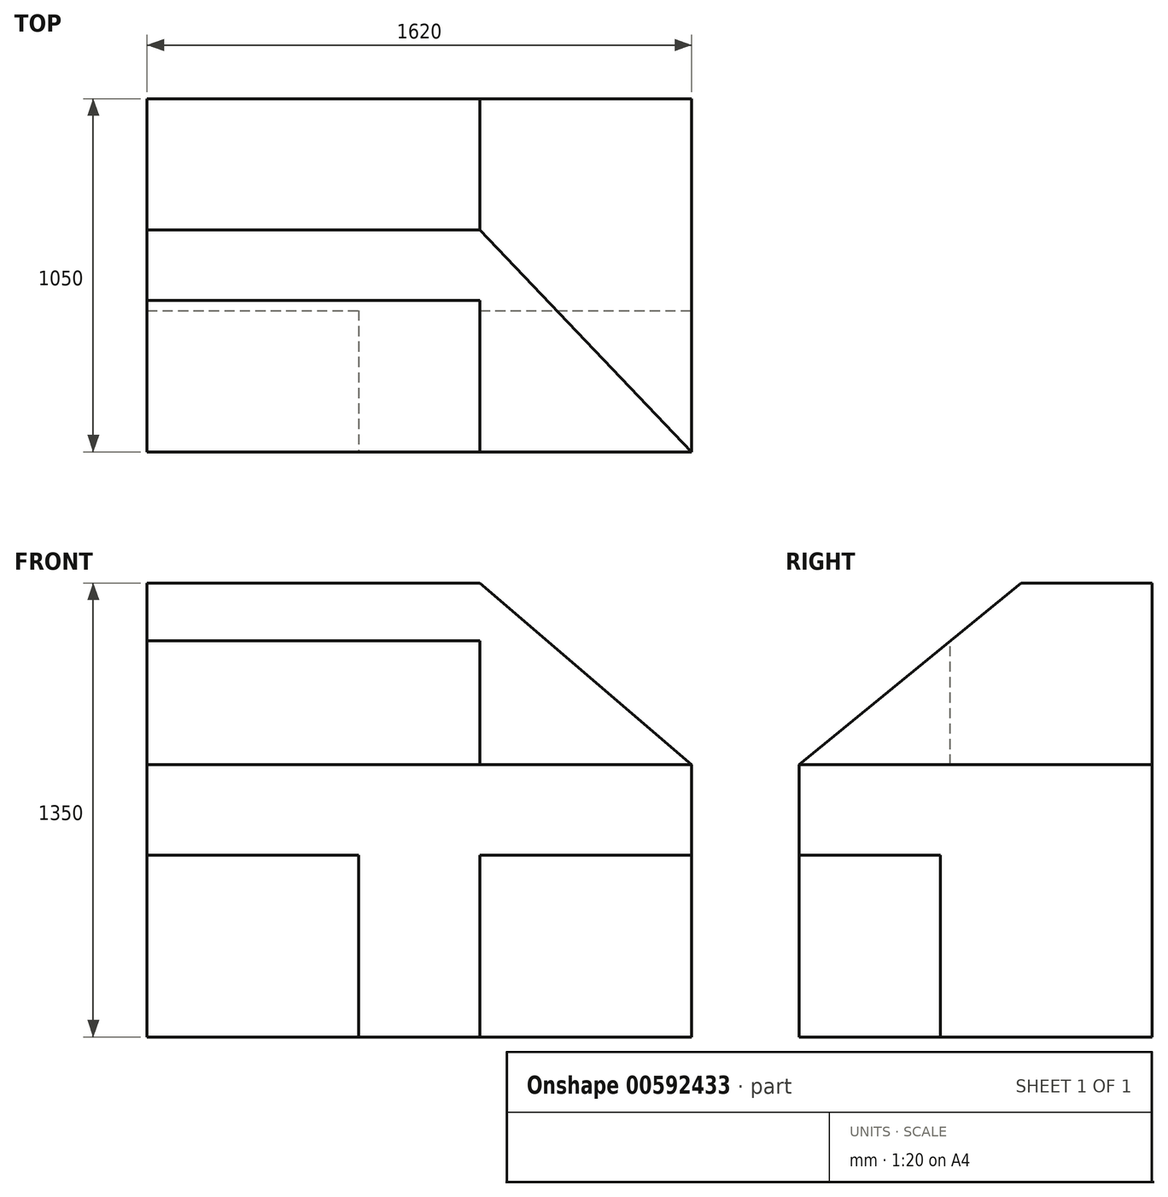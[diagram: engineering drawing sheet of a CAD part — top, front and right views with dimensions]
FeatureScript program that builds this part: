
annotation { "Feature Type Name" : "Feature", "Feature Type Description" : "" }
export const myFeature = defineFeature(function(context is Context, id is Id, definition is map)
    precondition{}
    {
        {
            var Q0;
            Q0=qCreatedBy(makeId("Front.planeOp"),FACE);
            var sketch = newSketch(context, id + "F0", { "sketchPlane" : qUnion([Q0])});
            skLineSegment(sketch, "E0.bottom", {"start": v(-810, 675) * mm, "end": v(810, 675) * mm});
            skLineSegment(sketch, "E0.top", {"start": v(-810, -675) * mm, "end": v(810, -675) * mm});
            skLineSegment(sketch, "E0.left", {"start": v(-810, 675) * mm, "end": v(-810, -675) * mm});
            skLineSegment(sketch, "E0.right", {"start": v(810, 675) * mm, "end": v(810, -675) * mm});
            skSolve(sketch);
        }
        {
            var Q0;
            Q0 = qSketchRegion(id + "F0", true);
            extrude(context, id + "F1", {"entities" : qUnion([Q0]), "depth" : 1050 * mm, "offsetDistance" : 25 * mm, "symmetric" : true});
        }
        {
            var Q0;
            Q0=makeQuery(id+"F1.opExtrude","CAP_FACE",FACE,{"disambiguationData":[OSD([sQuery(id+"F0.wireOp",EDGE,"E0.bottom"),sQuery(id+"F0.wireOp",EDGE,"E0.top"),sQuery(id+"F0.wireOp",EDGE,"E0.left"),sQuery(id+"F0.wireOp",EDGE,"E0.right")])],"isStart":false});
            var sketch = newSketch(context, id + "F2", { "sketchPlane" : qUnion([Q0])});
            skLineSegment(sketch, "E1.bottom", {"start": v(-810, -675) * mm, "end": v(-180, -675) * mm});
            skLineSegment(sketch, "E1.top", {"start": v(-810, -135) * mm, "end": v(-180, -135) * mm});
            skLineSegment(sketch, "E1.left", {"start": v(-810, -675) * mm, "end": v(-810, -135) * mm});
            skLineSegment(sketch, "E1.right", {"start": v(-180, -675) * mm, "end": v(-180, -135) * mm});
            skLineSegment(sketch, "E2.bottom", {"start": v(810, -675) * mm, "end": v(180, -675) * mm});
            skLineSegment(sketch, "E2.top", {"start": v(810, -135) * mm, "end": v(180, -135) * mm});
            skLineSegment(sketch, "E2.left", {"start": v(810, -675) * mm, "end": v(810, -135) * mm});
            skLineSegment(sketch, "E2.right", {"start": v(180, -675) * mm, "end": v(180, -135) * mm});
            skSolve(sketch);
        }
        {
            var Q0;
            Q0 = qSketchRegion(id + "F2", true);
            extrude(context, id + "F3", {"entities" : qUnion([Q0]), "operationType" : NewBodyOperationType.REMOVE, "oppositeDirection" : true, "depth" : 420 * mm, "offsetDistance" : 25 * mm});
        }
        {
            var Q0;
            Q0=makeQuery(id+"F1.opExtrude","SWEPT_FACE",FACE,{"disambiguationData":[OSD([sQuery(id+"F0.wireOp",EDGE,"E0.bottom")])]});
            var sketch = newSketch(context, id + "F4", { "sketchPlane" : qUnion([Q0])});
            skLineSegment(sketch, "E3.bottom", {"start": v(-810, -525) * mm, "end": v(180, -525) * mm});
            skLineSegment(sketch, "E3.top", {"start": v(-810, -75) * mm, "end": v(180, -75) * mm});
            skLineSegment(sketch, "E3.left", {"start": v(-810, -525) * mm, "end": v(-810, -75) * mm});
            skLineSegment(sketch, "E3.right", {"start": v(180, -525) * mm, "end": v(180, -75) * mm});
            skSolve(sketch);
        }
        {
            var Q0;
            Q0 = qSketchRegion(id + "F4", true);
            extrude(context, id + "F5", {"entities" : qUnion([Q0]), "operationType" : NewBodyOperationType.REMOVE, "oppositeDirection" : true, "depth" : 540 * mm, "offsetDistance" : 25 * mm});
        }
        {
            var Q0;
            Q0=makeQuery(id+"F1.opExtrude","SWEPT_FACE",FACE,{"disambiguationData":[OSD([sQuery(id+"F0.wireOp",EDGE,"E0.right")])]});
            var sketch = newSketch(context, id + "F6", { "sketchPlane" : qUnion([Q0])});
            skLineSegment(sketch, "E4", {"start": v(-525, 675) * mm, "end": v(-525, 135) * mm});
            skLineSegment(sketch, "E5", {"start": v(-525, 135) * mm, "end": v(135, 675) * mm});
            skLineSegment(sketch, "E6", {"start": v(135, 675) * mm, "end": v(-525, 675) * mm});
            skSolve(sketch);
        }
        {
            var Q0;
            Q0 = qSketchRegion(id + "F6", true);
            extrude(context, id + "F7", {"entities" : qUnion([Q0]), "operationType" : NewBodyOperationType.REMOVE, "endBound" : BoundingType.THROUGH_ALL, "oppositeDirection" : true, "depth" : 25 * mm, "offsetDistance" : 25 * mm});
        }
        {
            var Q0;
            Q0=makeQuery(id+"F1.opExtrude","CAP_FACE",FACE,{"disambiguationData":[OSD([sQuery(id+"F0.wireOp",EDGE,"E0.bottom"),sQuery(id+"F0.wireOp",EDGE,"E0.top"),sQuery(id+"F0.wireOp",EDGE,"E0.left"),sQuery(id+"F0.wireOp",EDGE,"E0.right")])],"isStart":false});
            var sketch = newSketch(context, id + "F8", { "sketchPlane" : qUnion([Q0])});
            skLineSegment(sketch, "E7", {"start": v(810, 135) * mm, "end": v(810, 675) * mm});
            skLineSegment(sketch, "E8", {"start": v(810, 675) * mm, "end": v(180, 675) * mm});
            skLineSegment(sketch, "E9", {"start": v(180, 675) * mm, "end": v(810, 135) * mm});
            skSolve(sketch);
        }
        {
            var Q0;
            Q0 = qSketchRegion(id + "F8", true);
            extrude(context, id + "F9", {"entities" : qUnion([Q0]), "operationType" : NewBodyOperationType.REMOVE, "endBound" : BoundingType.THROUGH_ALL, "oppositeDirection" : true, "depth" : 25 * mm, "offsetDistance" : 25 * mm});
        }
    });
